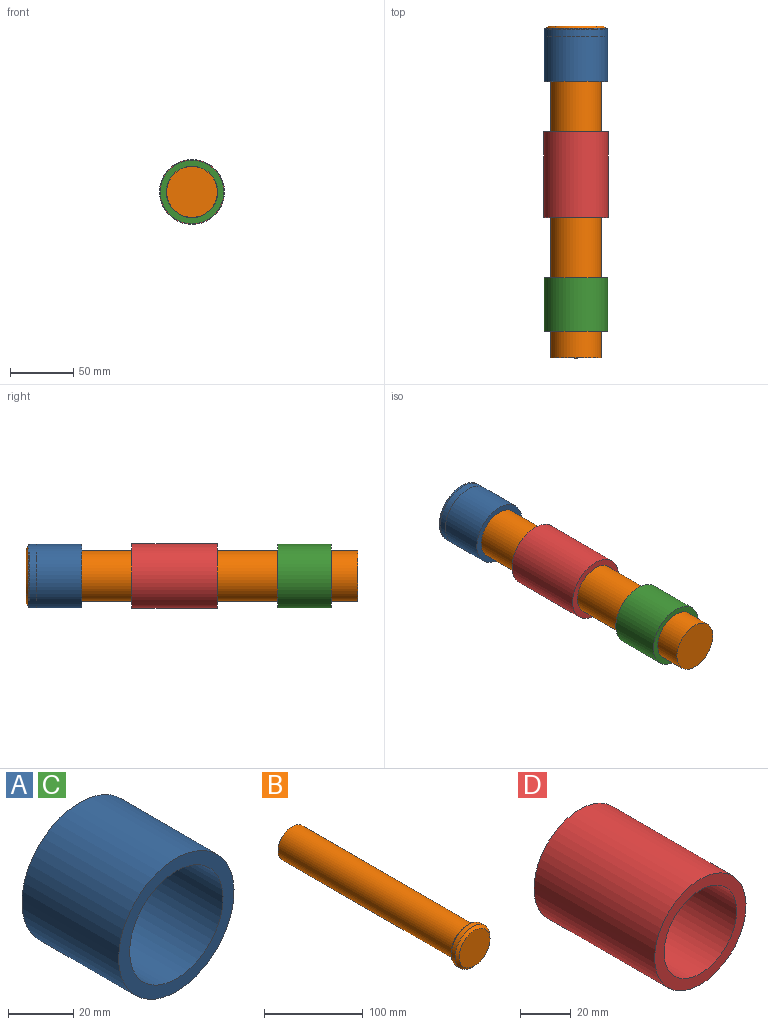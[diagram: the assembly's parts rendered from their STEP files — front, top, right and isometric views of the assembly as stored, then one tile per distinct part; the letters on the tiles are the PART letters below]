
ASSEMBLY  parts=4 mates=3
PART A: 4 faces, bbox 50.1x42x50.1 mm
  f0: cylinder r=20.28mm len=42mm, axis (0,1,0), area 5350.4mm2, adj f2,f3
  f1: cylinder r=25.05mm len=50.1mm, axis (0,1,0), area 6610.5mm2, adj f2,f3
  f2: plane 50.1x50.1mm, normal (0,-1,0), area 679.9mm2, adj f0,f1
  f3: plane 50.1x50.1mm, normal (0,1,0), area 679.9mm2, adj f0,f1
PART B: 7 faces, bbox 50x261.5x50 mm
  f0: cylinder r=20mm len=250mm, axis (0,1,0), area 31415.9mm2, adj f1,f4
  f1: plane 40x40mm, normal (0,1,0), area 1256.6mm2, adj f0
  f2: cylinder r=25mm len=50mm, axis (0,1,0), area 863.9mm2, adj f5,f6
  f3: plane 44x44mm, normal (0,-1,0), area 1520.5mm2, adj f5
  f4: plane 44x44mm, normal (0,1,0), area 263.9mm2, adj f0,f6
  f5: cone r=22mm half-angle=45deg, axis (0,1,0), area 626.4mm2, adj f2,f3
  f6: cone r=25mm half-angle=45deg, axis (0,-1,0), area 626.4mm2, adj f2,f4
PART C: same geometry as A
PART D: 4 faces, bbox 51.1x67.5x51.1 mm
  f0: cylinder r=20.28mm len=67.5mm, axis (0,1,0), area 8598.9mm2, adj f2,f3
  f1: cylinder r=25.55mm len=67.5mm, axis (0,1,0), area 10836.1mm2, adj f2,f3
  f2: plane 51.1x51.1mm, normal (0,-1,0), area 759.4mm2, adj f0,f1
  f3: plane 51.1x51.1mm, normal (0,1,0), area 759.4mm2, adj f0,f1
PLACE A t=(-147.78,-22.3,14.39)mm
PLACE B rot(axis=(1,0,0),180deg) t=(-147.78,-282.09,14.39)mm
PLACE C t=(-147.78,-219.05,14.39)mm
PLACE D t=(-147.78,-103.92,14.39)mm
MATE slider B.f0 <-> D.f1  axis (0,-1,0) through (-147.78,-157.09,14.39)mm
MATE slider C.f1 <-> B.f0  axis (0,1,0) through (-147.78,-261.05,14.39)mm
MATE slider A.f0 <-> B.f0  axis (0,1,0) through (-147.78,-64.3,14.39)mm
